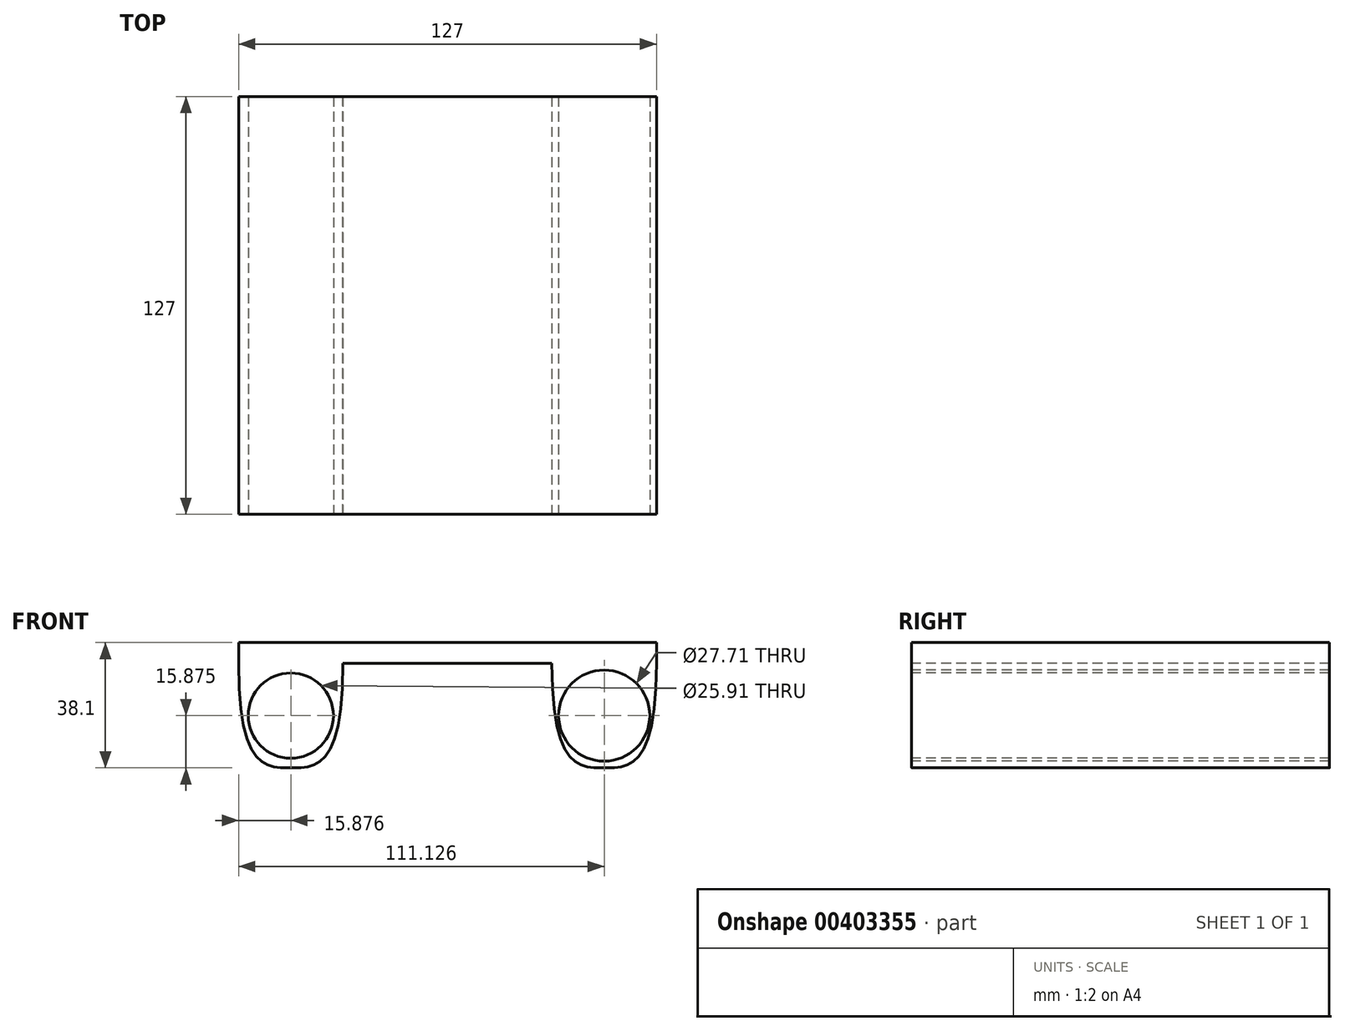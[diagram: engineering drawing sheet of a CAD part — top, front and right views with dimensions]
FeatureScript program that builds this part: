
annotation { "Feature Type Name" : "Feature", "Feature Type Description" : "" }
export const myFeature = defineFeature(function(context is Context, id is Id, definition is map)
    precondition{}
    {
        {
            var Q0;
            Q0=qCreatedBy(makeId("Front.planeOp"),FACE);
            var sketch = newSketch(context, id + "F0", { "sketchPlane" : qUnion([Q0])});
            skLineSegment(sketch, "E0.bottom", {"start": v(-75.69, 0) * mm, "end": v(51.31, 0) * mm});
            skLineSegment(sketch, "E0.top", {"start": v(-75.69, 6.35) * mm, "end": v(51.31, 6.35) * mm});
            skLineSegment(sketch, "E0.left", {"start": v(-75.69, 0) * mm, "end": v(-75.69, 6.35) * mm});
            skLineSegment(sketch, "E0.right", {"start": v(51.31, 0) * mm, "end": v(51.31, 6.35) * mm});
            skFitSpline(sketch, "E1", {"points": [v(51.31, 0) * mm, v(35.44, -31.75) * mm, v(19.56, 0) * mm], "startDerivative": vector(0, -190.5) * mm, "endDerivative": vector(0, 190.5) * mm});
            skFitSpline(sketch, "E2", {"points": [v(-75.69, 0) * mm, v(-59.81, -31.75) * mm, v(-43.94, 0) * mm], "startDerivative": vector(0.05, -190.5) * mm, "endDerivative": vector(-0.05, 190.5) * mm});
            skSolve(sketch);
        }
        {
            var Q0;
            Q0=makeQuery(id+"F0.imprint","IMPRINT",FACE,{"disambiguationData":[TD([[makeQuery(id+"F0.imprint","IMPRINT",EDGE,{"derivedFrom":sQuery(id+"F0.wireOp",EDGE,"E0.top")}),-1.0]])]});
            extrude(context, id + "F1", {"entities" : qUnion([Q0]), "oppositeDirection" : true, "depth" : 63.5 * mm});
        }
        {
            var Q0;
            Q0=makeQuery(id+"F1.opExtrude","CAP_EDGE",EDGE,{"disambiguationData":[OSD([sQuery(id+"F0.wireOp",EDGE,"E0.top")])],"isStart":false});
            cPlane(context, id + "F2", {"entities" : qUnion([Q0]), "cplaneType" : CPlaneType.LINE_ANGLE, "offset" : 25.4 * mm, "angle" : 0 * degree, "width" : 152.4 * mm, "height" : 152.4 * mm});
        }
        {
            var Q0;
            {var subQ0=sQuery(id+"F0.wireOp",EDGE,"E1");Q0=makeQuery(id+"F0.imprint","IMPRINT",FACE,{"disambiguationData":[TD([[makeQuery(id+"F0.imprint","IMPRINT",EDGE,{"derivedFrom":subQ0}),-1.0]])]});}
            var Q1;
            {var subQ0=sQuery(id+"F0.wireOp",EDGE,"E2");Q1=makeQuery(id+"F0.imprint","IMPRINT",FACE,{"disambiguationData":[TD([[makeQuery(id+"F0.imprint","IMPRINT",EDGE,{"derivedFrom":subQ0}),1.0]])]});}
            extrude(context, id + "F3", {"entities" : qUnion([Q0, Q1]), "operationType" : NewBodyOperationType.ADD, "oppositeDirection" : true, "depth" : 63.5 * mm});
        }
        {
            var Q0;
            Q0=makeQuery(id+"F1.opExtrude","SWEPT_BODY",BODY,{"disambiguationData":[OSD([sQuery(id+"F0.wireOp",EDGE,"E0.bottom"),sQuery(id+"F0.wireOp",EDGE,"E0.top"),sQuery(id+"F0.wireOp",EDGE,"E0.left"),sQuery(id+"F0.wireOp",EDGE,"E0.right")])]});
            var Q1;
            Q1=qCreatedBy(id+"F2.planeOp",FACE);
            mirror(context, id + "F4", {"operationType" : NewBodyOperationType.ADD, "entities" : qUnion([Q0]), "mirrorPlane" : qUnion([Q1])});
        }
        {
            var Q0;
            {var subQ0=sQuery(id+"F0.wireOp",EDGE,"E1");Q0=makeQuery(id+"F0.imprint","IMPRINT",FACE,{"disambiguationData":[TD([[makeQuery(id+"F0.imprint","IMPRINT",EDGE,{"derivedFrom":subQ0}),-1.0]])]});}
            var sketch = newSketch(context, id + "F5", { "sketchPlane" : qUnion([Q0])});
            skCircle(sketch, "E3", {"center": v(35.44, -15.88) * mm, "radius": 13.85 * mm});
            skSolve(sketch);
        }
        {
            var Q0;
            Q0=qSketchRegion(id+"F5",true);
            extrude(context, id + "F6", {"entities" : qUnion([Q0]), "operationType" : NewBodyOperationType.REMOVE, "oppositeDirection" : true, "depth" : 127 * mm});
        }
        {
            var Q0;
            {var subQ0=sQuery(id+"F0.wireOp",EDGE,"E2");Q0=makeQuery(id+"F0.imprint","IMPRINT",FACE,{"disambiguationData":[TD([[makeQuery(id+"F0.imprint","IMPRINT",EDGE,{"derivedFrom":subQ0}),1.0]])]});}
            var sketch = newSketch(context, id + "F7", { "sketchPlane" : qUnion([Q0])});
            skCircle(sketch, "E4", {"center": v(-59.81, -15.88) * mm, "radius": 12.95 * mm});
            skSolve(sketch);
        }
        {
            var Q0;
            Q0=qSketchRegion(id+"F7",true);
            extrude(context, id + "F8", {"entities" : qUnion([Q0]), "operationType" : NewBodyOperationType.REMOVE, "oppositeDirection" : true, "depth" : 127 * mm});
        }
    });
